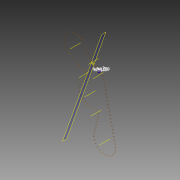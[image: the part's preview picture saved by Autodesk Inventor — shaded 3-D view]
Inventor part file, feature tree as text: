
AUTODESK INVENTOR PART (.ipt)
format: ipt  version: 2014 SP1 (Build 180222100, 222)  size: 438,784 bytes
history: native  units: mm (DEFAULTED — no unit token found)
features: other x95, extrude x85, sketch x2, plane x1, pattern_linear x1
ambient origin geometry x8: Origin, YZ Plane, XZ Plane, XY Plane, X Axis, Y Axis, Z Axis, Center Point
bodies: Body1 (feature_tree), Body2 (feature_tree), Body3 (feature_tree), Body4 (feature_tree), Body5 (feature_tree), Body6 (feature_tree), Body7 (feature_tree), Body8 (feature_tree), Body9 (feature_tree), Body10 (feature_tree), Body11 (feature_tree), Body12 (feature_tree), Body13 (feature_tree), Body14 (feature_tree), Body15 (feature_tree), Body16 (feature_tree), Body17 (feature_tree), Body18 (feature_tree), Body19 (feature_tree), Body20 (feature_tree), Body21 (feature_tree), Body22 (feature_tree), Body23 (feature_tree), Body24 (feature_tree), Body25 (feature_tree), Body26 (feature_tree), Body27 (feature_tree), Body28 (feature_tree), Body29 (feature_tree), Body30 (feature_tree), Body31 (feature_tree), Body32 (feature_tree), Body33 (feature_tree), Body34 (feature_tree), Body35 (feature_tree), Body36 (feature_tree), Body37 (feature_tree), Body38 (feature_tree), Body39 (feature_tree), Body40 (feature_tree), Body41 (feature_tree), Body42 (feature_tree), Body43 (feature_tree), Body44 (feature_tree), Body45 (feature_tree), Body46 (feature_tree), Body47 (feature_tree), Body48 (feature_tree), Body49 (feature_tree), Body50 (feature_tree), Body51 (feature_tree), Body52 (feature_tree), Body53 (feature_tree), Body54 (feature_tree), Body55 (feature_tree), Body56 (feature_tree), Body57 (feature_tree), Body58 (feature_tree), Body59 (feature_tree), Body60 (feature_tree), Body61 (feature_tree), Body62 (feature_tree), Body63 (feature_tree), Body64 (feature_tree), Body65 (feature_tree), Body66 (feature_tree), Body67 (feature_tree), Body68 (feature_tree), Body69 (feature_tree), Body70 (feature_tree), Body71 (feature_tree), Body72 (feature_tree), Body73 (feature_tree), Body74 (feature_tree), Body75 (feature_tree), Body76 (feature_tree), Body77 (feature_tree), Body78 (feature_tree), Body79 (feature_tree), Body80 (feature_tree), Body81 (feature_tree), Body82 (feature_tree), Body83 (feature_tree), Body84 (feature_tree), Body85 (feature_tree)
feature tree (184):
  sketch  "Sketch Path"  dims[d1=10.6172mm d2=7.9375mm d3=2.682204mm d5=6.981317mm d7=0.0mm d8=0.0mm d10=0.0mm d11=0.0mm d12=0.0mm d13=0.0mm d14=0.0mm d15=0.0mm d16=2.54mm d17=0.0mm d18=850.0mm]
  other  "Cross Section Plane"
  other  "Work Axis1"
  other  "Work Axis3"
  other  "Work Axis4"
  other  "Work Axis5"
  other  "Work Axis6"
  other  "Work Axis7"
  other  "Work Axis8"
  other  "Cross Section"
  other  "Work Point1"
  plane  "Work Plane2"
  pattern_linear  "Rectangular Pattern1"  Spacing1=7.9375mm  [1 undecoded]
  sketch  "Sketch3"  dims[d0=0.0mm]
  other  "Srf1"
  other  "Srf2"
  other  "Srf3"
  other  "Srf4"
  other  "Srf5"
  other  "Srf6"
  other  "Srf7"
  other  "Srf8"
  other  "Srf9"
  other  "Srf10"
  other  "Srf11"
  other  "Srf12"
  other  "Srf13"
  other  "Srf14"
  other  "Srf15"
  other  "Srf16"
  other  "Srf17"
  other  "Srf18"
  other  "Srf19"
  other  "Srf20"
  other  "Srf21"
  other  "Srf22"
  other  "Srf23"
  other  "Srf24"
  other  "Srf25"
  other  "Srf26"
  other  "Srf27"
  other  "Srf28"
  other  "Srf29"
  other  "Srf30"
  other  "Srf31"
  other  "Srf32"
  other  "Srf33"
  other  "Srf34"
  other  "Srf35"
  other  "Srf36"
  other  "Srf37"
  other  "Srf38"
  other  "Srf39"
  other  "Srf40"
  other  "Srf41"
  other  "Srf42"
  other  "Srf43"
  other  "Srf44"
  other  "Srf45"
  other  "Srf46"
  other  "Srf47"
  other  "Srf48"
  other  "Srf49"
  other  "Srf50"
  other  "Srf51"
  other  "Srf52"
  other  "Srf53"
  other  "Srf54"
  other  "Srf55"
  other  "Srf56"
  other  "Srf57"
  other  "Srf58"
  other  "Srf59"
  other  "Srf60"
  other  "Srf61"
  other  "Srf62"
  other  "Srf63"
  other  "Srf64"
  other  "Srf65"
  other  "Srf66"
  other  "Srf67"
  other  "Srf68"
  other  "Srf69"
  other  "Srf70"
  other  "Srf71"
  other  "Srf72"
  other  "Srf73"
  other  "Srf74"
  other  "Srf75"
  other  "Srf76"
  other  "Srf77"
  other  "Srf78"
  other  "Srf79"
  other  "Srf80"
  other  "Srf81"
  other  "Srf82"
  other  "Srf83"
  other  "Srf84"
  other  "Srf85"
  extrude  "ExtrusionSrf1"  Depth=2.682204mm
  extrude  "ExtrusionSrf2"  Depth=6.981317mm
  extrude  "ExtrusionSrf3"  TaperAngle=0.0deg  [1 undecoded]
  extrude  "ExtrusionSrf4"  Depth=2.54mm TaperAngle=0.0deg
  extrude  "ExtrusionSrf5"  Depth=850.0mm
  extrude  "ExtrusionSrf6"  [1 undecoded]
  extrude  "ExtrusionSrf7"  [1 undecoded]
  extrude  "ExtrusionSrf8"  [1 undecoded]
  extrude  "ExtrusionSrf9"  [1 undecoded]
  extrude  "ExtrusionSrf10"  [1 undecoded]
  extrude  "ExtrusionSrf11"  [1 undecoded]
  extrude  "ExtrusionSrf12"  [1 undecoded]
  extrude  "ExtrusionSrf13"  [1 undecoded]
  extrude  "ExtrusionSrf14"  [1 undecoded]
  extrude  "ExtrusionSrf15"  [1 undecoded]
  extrude  "ExtrusionSrf16"  [1 undecoded]
  extrude  "ExtrusionSrf17"  [1 undecoded]
  extrude  "ExtrusionSrf18"  [1 undecoded]
  extrude  "ExtrusionSrf19"  [1 undecoded]
  extrude  "ExtrusionSrf20"  [1 undecoded]
  extrude  "ExtrusionSrf21"  [1 undecoded]
  extrude  "ExtrusionSrf22"  [1 undecoded]
  extrude  "ExtrusionSrf23"  [1 undecoded]
  extrude  "ExtrusionSrf24"  [1 undecoded]
  extrude  "ExtrusionSrf25"  [1 undecoded]
  extrude  "ExtrusionSrf26"  [1 undecoded]
  extrude  "ExtrusionSrf27"  [1 undecoded]
  extrude  "ExtrusionSrf28"  [1 undecoded]
  extrude  "ExtrusionSrf29"  [1 undecoded]
  extrude  "ExtrusionSrf30"  [1 undecoded]
  extrude  "ExtrusionSrf31"  [1 undecoded]
  extrude  "ExtrusionSrf32"  [1 undecoded]
  extrude  "ExtrusionSrf33"  [1 undecoded]
  extrude  "ExtrusionSrf34"  [1 undecoded]
  extrude  "ExtrusionSrf35"  [1 undecoded]
  extrude  "ExtrusionSrf36"  [1 undecoded]
  extrude  "ExtrusionSrf37"  [1 undecoded]
  extrude  "ExtrusionSrf38"  [1 undecoded]
  extrude  "ExtrusionSrf39"  [1 undecoded]
  extrude  "ExtrusionSrf40"  [1 undecoded]
  extrude  "ExtrusionSrf41"  [1 undecoded]
  extrude  "ExtrusionSrf42"  [1 undecoded]
  extrude  "ExtrusionSrf43"  [1 undecoded]
  extrude  "ExtrusionSrf44"  [1 undecoded]
  extrude  "ExtrusionSrf45"  [1 undecoded]
  extrude  "ExtrusionSrf46"  [1 undecoded]
  extrude  "ExtrusionSrf47"  [1 undecoded]
  extrude  "ExtrusionSrf48"  [1 undecoded]
  extrude  "ExtrusionSrf49"  [1 undecoded]
  extrude  "ExtrusionSrf50"  [1 undecoded]
  extrude  "ExtrusionSrf51"  [1 undecoded]
  extrude  "ExtrusionSrf52"  [1 undecoded]
  extrude  "ExtrusionSrf53"  [1 undecoded]
  extrude  "ExtrusionSrf54"  [1 undecoded]
  extrude  "ExtrusionSrf55"  [1 undecoded]
  extrude  "ExtrusionSrf56"  [1 undecoded]
  extrude  "ExtrusionSrf57"  [1 undecoded]
  extrude  "ExtrusionSrf58"  [1 undecoded]
  extrude  "ExtrusionSrf59"  [1 undecoded]
  extrude  "ExtrusionSrf60"  [1 undecoded]
  extrude  "ExtrusionSrf61"  [1 undecoded]
  extrude  "ExtrusionSrf62"  [1 undecoded]
  extrude  "ExtrusionSrf63"  [1 undecoded]
  extrude  "ExtrusionSrf64"  [1 undecoded]
  extrude  "ExtrusionSrf65"  [1 undecoded]
  extrude  "ExtrusionSrf66"  [1 undecoded]
  extrude  "ExtrusionSrf67"  [1 undecoded]
  extrude  "ExtrusionSrf68"  [1 undecoded]
  extrude  "ExtrusionSrf69"  [1 undecoded]
  extrude  "ExtrusionSrf70"  [1 undecoded]
  extrude  "ExtrusionSrf71"  [1 undecoded]
  extrude  "ExtrusionSrf72"  [1 undecoded]
  extrude  "ExtrusionSrf73"  [1 undecoded]
  extrude  "ExtrusionSrf74"  [1 undecoded]
  extrude  "ExtrusionSrf75"  [1 undecoded]
  extrude  "ExtrusionSrf76"  [1 undecoded]
  extrude  "ExtrusionSrf77"  [1 undecoded]
  extrude  "ExtrusionSrf78"  [1 undecoded]
  extrude  "ExtrusionSrf79"  [1 undecoded]
  extrude  "ExtrusionSrf80"  [1 undecoded]
  extrude  "ExtrusionSrf81"  [1 undecoded]
  extrude  "ExtrusionSrf82"  [1 undecoded]
  extrude  "ExtrusionSrf83"  [1 undecoded]
  extrude  "ExtrusionSrf84"  [1 undecoded]
  extrude  "ExtrusionSrf85"  [1 undecoded]
note: 82 required parameter values undecoded (feature->parameter linkage not recoverable at this tier; creation-order binding heuristic only, values carry confidence <= 0.55)
